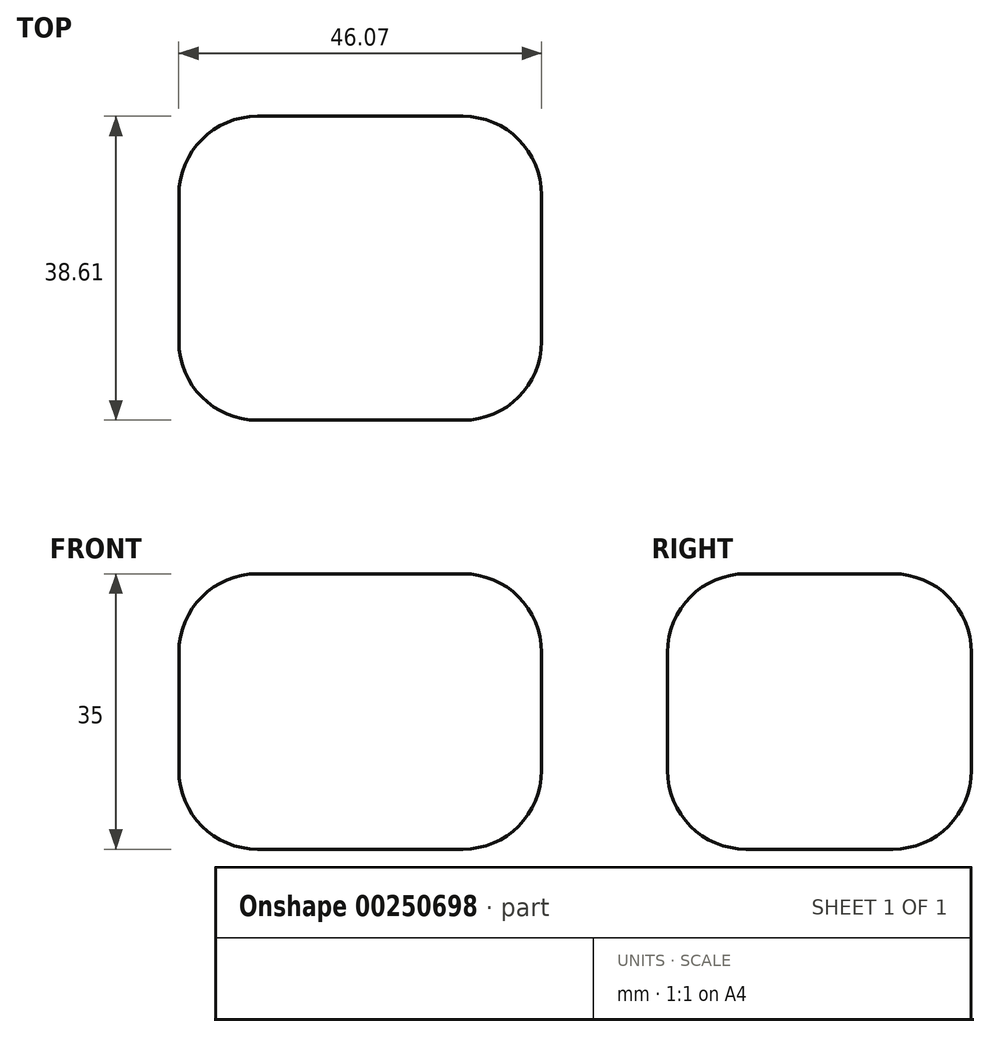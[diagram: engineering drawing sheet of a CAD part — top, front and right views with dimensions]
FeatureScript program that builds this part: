
annotation { "Feature Type Name" : "Feature", "Feature Type Description" : "" }
export const myFeature = defineFeature(function(context is Context, id is Id, definition is map)
    precondition{}
    {
        {
            var Q0;
            Q0=qCreatedBy(makeId("Top.planeOp"),FACE);
            var sketch = newSketch(context, id + "F0", { "sketchPlane" : qUnion([Q0])});
            skLineSegment(sketch, "E0.bottom", {"start": v(-58.8, 51.34) * mm, "end": v(-12.73, 51.34) * mm});
            skLineSegment(sketch, "E0.top", {"start": v(-58.8, 12.73) * mm, "end": v(-12.73, 12.73) * mm});
            skLineSegment(sketch, "E0.left", {"start": v(-58.8, 51.34) * mm, "end": v(-58.8, 12.73) * mm});
            skLineSegment(sketch, "E0.right", {"start": v(-12.73, 51.34) * mm, "end": v(-12.73, 12.73) * mm});
            skSolve(sketch);
        }
        {
            var Q0;
            Q0 = qSketchRegion(id + "F0", true);
            extrude(context, id + "F1", {"entities" : qUnion([Q0]), "depth" : 25 * mm});
        }
        {
            var Q0;
            Q0=makeQuery(id+"F1.opExtrude","CAP_FACE",FACE,{"disambiguationData":[OSD([sQuery(id+"F0.wireOp",EDGE,"E0.bottom"),sQuery(id+"F0.wireOp",EDGE,"E0.top"),sQuery(id+"F0.wireOp",EDGE,"E0.left"),sQuery(id+"F0.wireOp",EDGE,"E0.right")])],"isStart":false});
            extrude(context, id + "F2", {"entities" : qUnion([Q0]), "operationType" : NewBodyOperationType.ADD, "depth" : 10 * mm});
        }
        {
            var Q0;
            Q0=makeQuery(id+"F2.opExtrude","CAP_EDGE",EDGE,{"disambiguationData":[OSD([sQuery(id+"F0.wireOp",EDGE,"E0.bottom")])],"isStart":false});
            var Q1;
            {var subQ0=sQuery(id+"F0.wireOp",EDGE,"E0.left");var subQ1=sQuery(id+"F0.wireOp",EDGE,"E0.bottom");Q1=makeQuery(id+"F2.boolean.opBoolean","MERGE",EDGE,{"derivedFrom":[makeQuery(id+"F1.opExtrude","SWEPT_EDGE",EDGE,{"disambiguationData":[OSD([subQ1,subQ0])]}),makeQuery(id+"F2.opExtrude","SWEPT_EDGE",EDGE,{"disambiguationData":[OSD([subQ1,subQ0])]})]});}
            var Q2;
            Q2=makeQuery(id+"F2.opExtrude","CAP_EDGE",EDGE,{"disambiguationData":[OSD([sQuery(id+"F0.wireOp",EDGE,"E0.left")])],"isStart":false});
            var Q3;
            {var subQ0=sQuery(id+"F0.wireOp",EDGE,"E0.left");var subQ1=sQuery(id+"F0.wireOp",EDGE,"E0.top");Q3=makeQuery(id+"F2.boolean.opBoolean","MERGE",EDGE,{"derivedFrom":[makeQuery(id+"F1.opExtrude","SWEPT_EDGE",EDGE,{"disambiguationData":[OSD([subQ1,subQ0])]}),makeQuery(id+"F2.opExtrude","SWEPT_EDGE",EDGE,{"disambiguationData":[OSD([subQ1,subQ0])]})]});}
            var Q4;
            Q4=makeQuery(id+"F1.opExtrude","CAP_EDGE",EDGE,{"disambiguationData":[OSD([sQuery(id+"F0.wireOp",EDGE,"E0.left")])],"isStart":true});
            var Q5;
            Q5=makeQuery(id+"F1.opExtrude","CAP_EDGE",EDGE,{"disambiguationData":[OSD([sQuery(id+"F0.wireOp",EDGE,"E0.bottom")])],"isStart":true});
            var Q6;
            {var subQ0=sQuery(id+"F0.wireOp",EDGE,"E0.right");var subQ1=sQuery(id+"F0.wireOp",EDGE,"E0.bottom");Q6=makeQuery(id+"F2.boolean.opBoolean","MERGE",EDGE,{"derivedFrom":[makeQuery(id+"F1.opExtrude","SWEPT_EDGE",EDGE,{"disambiguationData":[OSD([subQ1,subQ0])]}),makeQuery(id+"F2.opExtrude","SWEPT_EDGE",EDGE,{"disambiguationData":[OSD([subQ1,subQ0])]})]});}
            var Q7;
            Q7=makeQuery(id+"F2.opExtrude","CAP_EDGE",EDGE,{"disambiguationData":[OSD([sQuery(id+"F0.wireOp",EDGE,"E0.right")])],"isStart":false});
            var Q8;
            Q8=makeQuery(id+"F1.opExtrude","CAP_EDGE",EDGE,{"disambiguationData":[OSD([sQuery(id+"F0.wireOp",EDGE,"E0.right")])],"isStart":true});
            var Q9;
            {var subQ0=sQuery(id+"F0.wireOp",EDGE,"E0.right");var subQ1=sQuery(id+"F0.wireOp",EDGE,"E0.top");Q9=makeQuery(id+"F2.boolean.opBoolean","MERGE",EDGE,{"derivedFrom":[makeQuery(id+"F1.opExtrude","SWEPT_EDGE",EDGE,{"disambiguationData":[OSD([subQ1,subQ0])]}),makeQuery(id+"F2.opExtrude","SWEPT_EDGE",EDGE,{"disambiguationData":[OSD([subQ1,subQ0])]})]});}
            var Q10;
            Q10=makeQuery(id+"F2.opExtrude","CAP_EDGE",EDGE,{"disambiguationData":[OSD([sQuery(id+"F0.wireOp",EDGE,"E0.top")])],"isStart":false});
            var Q11;
            Q11=makeQuery(id+"F1.opExtrude","CAP_EDGE",EDGE,{"disambiguationData":[OSD([sQuery(id+"F0.wireOp",EDGE,"E0.top")])],"isStart":true});
            fillet(context, id + "F3", {"entities" : qUnion([Q0, Q1, Q2, Q3, Q4, Q5, Q6, Q7, Q8, Q9, Q10, Q11]), "radius" : 10 * mm, "tangentPropagation" : true, "allowEdgeOverflow" : false});
        }
    });
